# Revit family: ledfloodho-p-310w-4000-n_543017045600
name_source: partatom
category: Leuchten
revit_build: Autodesk Revit 2016 (Build: 20190508_0715(x64)
units: mm (PartAtom-declared; Revit-internal decimal feet)

## family parameters
Basisbauteil = Fläche
Beim Laden mit Abzugskörper schneiden = Nein
Bemaßung runder Anschluss = Durchmesser verwenden
Gemeinsam genutzt = Nein
Lichtquelle = Nein
Raumberechnungspunkt = Nein
Teiletyp = Normal

## types (1)
- LEDFloodHO-P-310W-4000-N (1 x LED, 40000 lm)
    Approval mark = CE, ENEC
    Beschreibung = Professional luminaire with special optics for area lighting. Including IP68 connector for easy connection. Up to 40% energy saving compared to HID solutions. Different optics to illuminate sport pitches (Class II/III NEN-EN 12193:2018) and open areas. Robust design: full IP66 and IK08 protection. Anodized aluminium heatsink, ideal for coastal environments.
    CIE Flux Codes = 89 96 99 99 100
    Control Gear = Electronic ballast
    Height = 169 mm
    Hersteller = OPPLE
    Lamp Light Flux = 40000 lm
    Lamp count = 1
    Lampe = 1 x LED
    Length = 472 mm
    Luminous efficacy = 129 lm/W
    ModVariant = Nein
    Modell = 543017045600
    Mounting Place = Wall
    Mounting Type = Surface mounted
    Number of Poles = 1
    OnlyDefault = Ja
    Power Factor = 1
    Product Name = LEDFloodHO-P-310W-4000-N
    Product group = Flood HO
    ProductGroupID = 2001
    Protection Class = Protection class I
    Protection Degree = IP 66
    RLX_Detail_Level = 1
    RlxData = <blob elided: 125669 chars, md5=3dc73173>
    Scheinlast = 310 VA
    Socket = socket
    Standby Power = 0 W
    System Light Flux = 39956 lm
    System Power = 310 W
    Typenbild = 543017045600.jpg
    Typenkommentare = Product without accessories
    URL = http://relux.com
    VarID = ---
    Voltage = 0 V
    Vorgabe-Ansicht = 1800 mm
    Weight = 0.00 kg
    Width = 448 mm

## geometry (parser evidence)
native form markers: Blend x4, Sweep x12
no freeform markers — native parametric forms only
